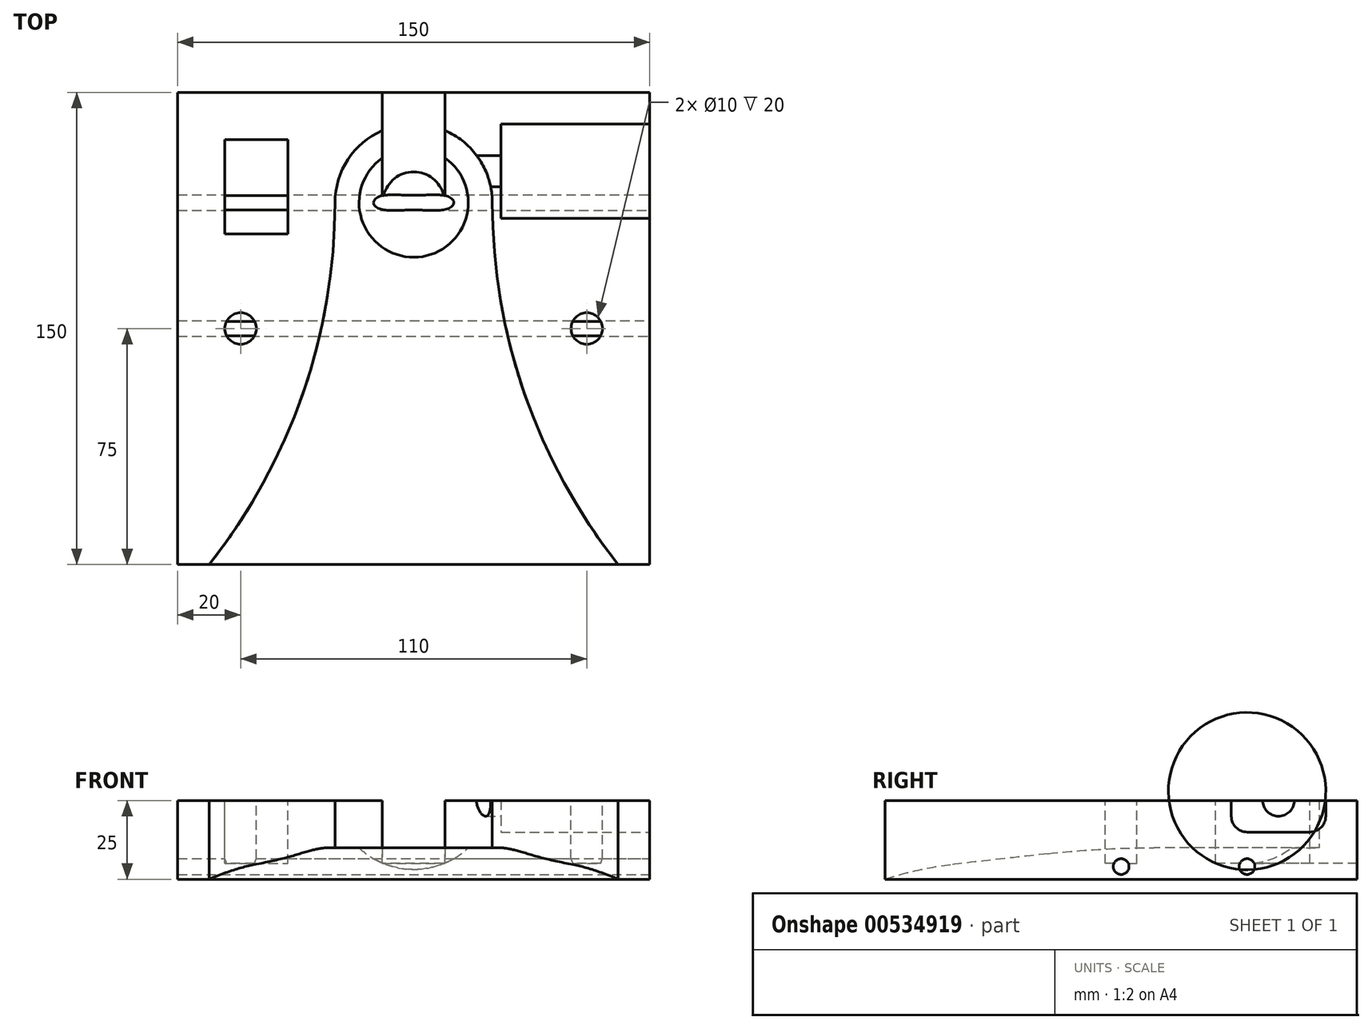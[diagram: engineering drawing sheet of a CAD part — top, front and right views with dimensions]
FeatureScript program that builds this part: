
annotation { "Feature Type Name" : "Feature", "Feature Type Description" : "" }
export const myFeature = defineFeature(function(context is Context, id is Id, definition is map)
    precondition{}
    {
        {
            var Q0;
            Q0=qCreatedBy(makeId("Top.planeOp"),FACE);
            var sketch = newSketch(context, id + "F0", { "sketchPlane" : qUnion([Q0])});
            skLineSegment(sketch, "E0.bottom", {"start": v(-75, 75) * mm, "end": v(75, 75) * mm});
            skLineSegment(sketch, "E0.top", {"start": v(-75, -75) * mm, "end": v(-65, -75) * mm});
            skLineSegment(sketch, "E0.left", {"start": v(-75, 75) * mm, "end": v(-75, -75) * mm});
            skLineSegment(sketch, "E0.right", {"start": v(75, 75) * mm, "end": v(75, -75) * mm});
            skLineSegment(sketch, "E1", {"start": v(75, 75) * mm, "end": v(-75, -75) * mm, "construction": true});
            skArc(sketch, "E2", {"start": v(25, 40) * mm, "mid": v(0, 65) * mm, "end": v(-25, 40) * mm});
            skLineSegment(sketch, "E3", {"start": v(0, 40) * mm, "end": v(75, 40) * mm, "construction": true});
            skLineSegment(sketch, "E4", {"start": v(75, 40) * mm, "end": v(-75, 40) * mm, "construction": true});
            skLineSegment(sketch, "E5", {"start": v(-25, 40) * mm, "end": v(-25, 75) * mm, "construction": true});
            skLineSegment(sketch, "E6", {"start": v(25, 40) * mm, "end": v(25, 75) * mm, "construction": true});
            skArc(sketch, "E7", {"start": v(-65, -75) * mm, "mid": v(-35.29, -20.88) * mm, "end": v(-25, 40) * mm});
            skArc(sketch, "E8", {"start": v(25, 40) * mm, "mid": v(35.29, -20.88) * mm, "end": v(65, -75) * mm});
            skLineSegment(sketch, "E9.trimOffspring", {"start": v(65, -75) * mm, "end": v(75, -75) * mm});
            skSolve(sketch);
        }
        {
            var Q0;
            Q0 = qSketchRegion(id + "F0", true);
            extrude(context, id + "F1", {"entities" : qUnion([Q0]), "depth" : 25 * mm, "offsetDistance" : 25 * mm});
        }
        {
            var Q0;
            Q0=makeQuery(id+"F1.opExtrude","SWEPT_FACE",FACE,{"disambiguationData":[OSD([sQuery(id+"F0.wireOp",EDGE,"E0.left")])]});
            var sketch = newSketch(context, id + "F2", { "sketchPlane" : qUnion([Q0])});
            skLineSegment(sketch, "E10", {"start": v(-75, 0) * mm, "end": v(-75, 10) * mm});
            skLineSegment(sketch, "E11", {"start": v(-75, 10) * mm, "end": v(-10.4, 10) * mm});
            skLineSegment(sketch, "E12", {"start": v(75, 0) * mm, "end": v(-75, 0) * mm});
            skArc(sketch, "E13", {"start": v(75, 0) * mm, "mid": v(64.74, 2.86) * mm, "end": v(54.23, 4.62) * mm});
            skArc(sketch, "E14", {"start": v(23.18, 8.12) * mm, "mid": v(6.42, 9.53) * mm, "end": v(-10.4, 10) * mm});
            skLineSegment(sketch, "E15", {"start": v(23.18, 8.12) * mm, "end": v(54.23, 4.62) * mm});
            skSolve(sketch);
        }
        {
            var Q0;
            Q0 = qSketchRegion(id + "F2", true);
            var Q1;
            Q1=makeQuery(id+"F1.opExtrude","SWEPT_FACE",FACE,{"disambiguationData":[OSD([sQuery(id+"F0.wireOp",EDGE,"E0.right")])]});
            extrude(context, id + "F3", {"entities" : qUnion([Q0]), "operationType" : NewBodyOperationType.ADD, "endBound" : BoundingType.UP_TO_SURFACE, "oppositeDirection" : true, "depth" : 25 * mm, "endBoundEntityFace" : qUnion([Q1]), "offsetDistance" : 25 * mm});
        }
        {
            var Q0;
            Q0=makeQuery(id+"F1.opExtrude","CAP_FACE",FACE,{"disambiguationData":[OSD([sQuery(id+"F0.wireOp",EDGE,"E0.bottom"),sQuery(id+"F0.wireOp",EDGE,"E0.top"),sQuery(id+"F0.wireOp",EDGE,"E0.left"),sQuery(id+"F0.wireOp",EDGE,"E0.right"),sQuery(id+"F0.wireOp",EDGE,"E2"),sQuery(id+"F0.wireOp",EDGE,"liNfy68U-UH0S-CfX7-c4kD-nzUfzZ1o6Ne9.bottom"),sQuery(id+"F0.wireOp",EDGE,"liNfy68U-UH0S-CfX7-c4kD-nzUfzZ1o6Ne9.top"),sQuery(id+"F0.wireOp",EDGE,"liNfy68U-UH0S-CfX7-c4kD-nzUfzZ1o6Ne9.left"),sQuery(id+"F0.wireOp",EDGE,"liNfy68U-UH0S-CfX7-c4kD-nzUfzZ1o6Ne9.right"),sQuery(id+"F0.wireOp",EDGE,"E7"),sQuery(id+"F0.wireOp",EDGE,"E8"),sQuery(id+"F0.wireOp",EDGE,"E9.trimOffspring")])],"isStart":false});
            cPlane(context, id + "F4", {"entities" : qUnion([Q0]), "cplaneType" : CPlaneType.OFFSET, "offset" : 3 * mm, "width" : 150 * mm, "height" : 150 * mm});
        }
        {
            var Q0;
            Q0=qCreatedBy(id+"F4.planeOp",FACE);
            var sketch = newSketch(context, id + "F5", { "sketchPlane" : qUnion([Q0])});
            skLineSegment(sketch, "E16", {"start": v(25, 40) * mm, "end": v(-25, 40) * mm, "construction": true});
            skArc(sketch, "E17", {"start": v(25, 40) * mm, "mid": v(0, 65) * mm, "end": v(-25, 40) * mm});
            skLineSegment(sketch, "E18", {"start": v(-25, 40) * mm, "end": v(25, 40) * mm});
            skSolve(sketch);
        }
        {
            var Q0;
            Q0 = qSketchRegion(id + "F5", true);
            var Q1;
            Q1=sQuery(id+"F5.wireOp",EDGE,"E16");
            revolve(context, id + "F6", {"operationType" : NewBodyOperationType.REMOVE, "entities" : qUnion([Q0]), "axis" : qUnion([Q1]), "revolveType" : RevolveType.FULL});
        }
        {
            var Q0;
            Q0=makeQuery(id+"F1.opExtrude","SWEPT_FACE",FACE,{"disambiguationData":[OSD([sQuery(id+"F0.wireOp",EDGE,"E0.right")])]});
            var sketch = newSketch(context, id + "F7", { "sketchPlane" : qUnion([Q0])});
            skCircle(sketch, "E19", {"center": v(40, 4) * mm, "radius": 2.5 * mm});
            skCircle(sketch, "E20", {"center": v(0, 4) * mm, "radius": 2.5 * mm});
            skLineSegment(sketch, "E21", {"start": v(0, 4) * mm, "end": v(40, 4) * mm, "construction": true});
            skSolve(sketch);
        }
        {
            var Q0;
            Q0 = qSketchRegion(id + "F7", true);
            extrude(context, id + "F8", {"entities" : qUnion([Q0]), "operationType" : NewBodyOperationType.REMOVE, "endBound" : BoundingType.THROUGH_ALL, "oppositeDirection" : true, "depth" : 100 * mm, "offsetDistance" : 25 * mm});
        }
        {
            var Q0;
            Q0=makeQuery(id+"F1.opExtrude","CAP_FACE",FACE,{"disambiguationData":[OSD([sQuery(id+"F0.wireOp",EDGE,"E0.bottom"),sQuery(id+"F0.wireOp",EDGE,"E0.top"),sQuery(id+"F0.wireOp",EDGE,"E0.left"),sQuery(id+"F0.wireOp",EDGE,"E0.right"),sQuery(id+"F0.wireOp",EDGE,"E2"),sQuery(id+"F0.wireOp",EDGE,"E7"),sQuery(id+"F0.wireOp",EDGE,"E8"),sQuery(id+"F0.wireOp",EDGE,"E9.trimOffspring")])],"isStart":false});
            var sketch = newSketch(context, id + "F9", { "sketchPlane" : qUnion([Q0])});
            skLineSegment(sketch, "E22.bottom", {"start": v(-60, 60) * mm, "end": v(-40, 60) * mm});
            skLineSegment(sketch, "E22.top", {"start": v(-60, 30) * mm, "end": v(-40, 30) * mm});
            skLineSegment(sketch, "E22.left", {"start": v(-60, 60) * mm, "end": v(-60, 30) * mm});
            skLineSegment(sketch, "E22.right", {"start": v(-40, 60) * mm, "end": v(-40, 30) * mm});
            skCircle(sketch, "E23", {"center": v(-55, 0) * mm, "radius": 5 * mm});
            skCircle(sketch, "E24", {"center": v(55, 0) * mm, "radius": 5 * mm});
            skLineSegment(sketch, "E25.bottom", {"start": v(-10, 75) * mm, "end": v(10, 75) * mm});
            skLineSegment(sketch, "E25.top", {"start": v(-10, 40) * mm, "end": v(10, 40) * mm});
            skLineSegment(sketch, "E25.left", {"start": v(-10, 75) * mm, "end": v(-10, 40) * mm});
            skLineSegment(sketch, "E25.right", {"start": v(10, 75) * mm, "end": v(10, 40) * mm});
            skLineSegment(sketch, "E26", {"start": v(0, 75) * mm, "end": v(0, 40) * mm, "construction": true});
            skSolve(sketch);
        }
        {
            var Q0;
            Q0 = qSketchRegion(id + "F9", true);
            extrude(context, id + "F10", {"entities" : qUnion([Q0]), "operationType" : NewBodyOperationType.REMOVE, "oppositeDirection" : true, "depth" : 20 * mm, "offsetDistance" : 25 * mm});
        }
        {
            var Q0;
            Q0=makeQuery(id+"F1.opExtrude","SWEPT_FACE",FACE,{"disambiguationData":[OSD([sQuery(id+"F0.wireOp",EDGE,"E0.right")])]});
            var sketch = newSketch(context, id + "F11", { "sketchPlane" : qUnion([Q0])});
            skLineSegment(sketch, "E27", {"start": v(35, 25) * mm, "end": v(35, 20) * mm});
            skLineSegment(sketch, "E28", {"start": v(40, 15) * mm, "end": v(60, 15) * mm});
            skLineSegment(sketch, "E29", {"start": v(65, 20) * mm, "end": v(65, 25) * mm});
            skPoint(sketch, "E30.visualSharp", {"position": v(35, 15) * mm});
            skArc(sketch, "E30.filletArc", {"start": v(35, 20) * mm, "mid": v(36.46, 16.46) * mm, "end": v(40, 15) * mm});
            skPoint(sketch, "E31.visualSharp", {"position": v(65, 15) * mm});
            skArc(sketch, "E31.filletArc", {"start": v(60, 15) * mm, "mid": v(63.54, 16.46) * mm, "end": v(65, 20) * mm});
            skLineSegment(sketch, "E32", {"start": v(35, 25) * mm, "end": v(65, 25) * mm});
            skSolve(sketch);
        }
        {
            var Q0;
            Q0 = qSketchRegion(id + "F11", true);
            extrude(context, id + "F12", {"entities" : qUnion([Q0]), "operationType" : NewBodyOperationType.REMOVE, "oppositeDirection" : true, "depth" : 47.3 * mm, "offsetDistance" : 25 * mm});
        }
        {
            var Q0;
            Q0=makeQuery(id+"F12.boolean.opBoolean","COPY",FACE,{"derivedFrom":makeQuery(id+"F12.opExtrude","CAP_FACE",FACE,{"disambiguationData":[OSD([sQuery(id+"F11.wireOp",EDGE,"E27"),sQuery(id+"F11.wireOp",EDGE,"E28"),sQuery(id+"F11.wireOp",EDGE,"E29"),sQuery(id+"F11.wireOp",EDGE,"E30.filletArc"),sQuery(id+"F11.wireOp",EDGE,"E31.filletArc"),sQuery(id+"F11.wireOp",EDGE,"E32")])],"isStart":false})});
            var sketch = newSketch(context, id + "F13", { "sketchPlane" : qUnion([Q0])});
            skCircle(sketch, "E33", {"center": v(50, 25) * mm, "radius": 5 * mm});
            skSolve(sketch);
        }
        {
            var Q0;
            Q0 = qSketchRegion(id + "F13", true);
            extrude(context, id + "F14", {"entities" : qUnion([Q0]), "operationType" : NewBodyOperationType.REMOVE, "oppositeDirection" : true, "depth" : 15.8 * mm, "offsetDistance" : 25 * mm});
        }
    });
